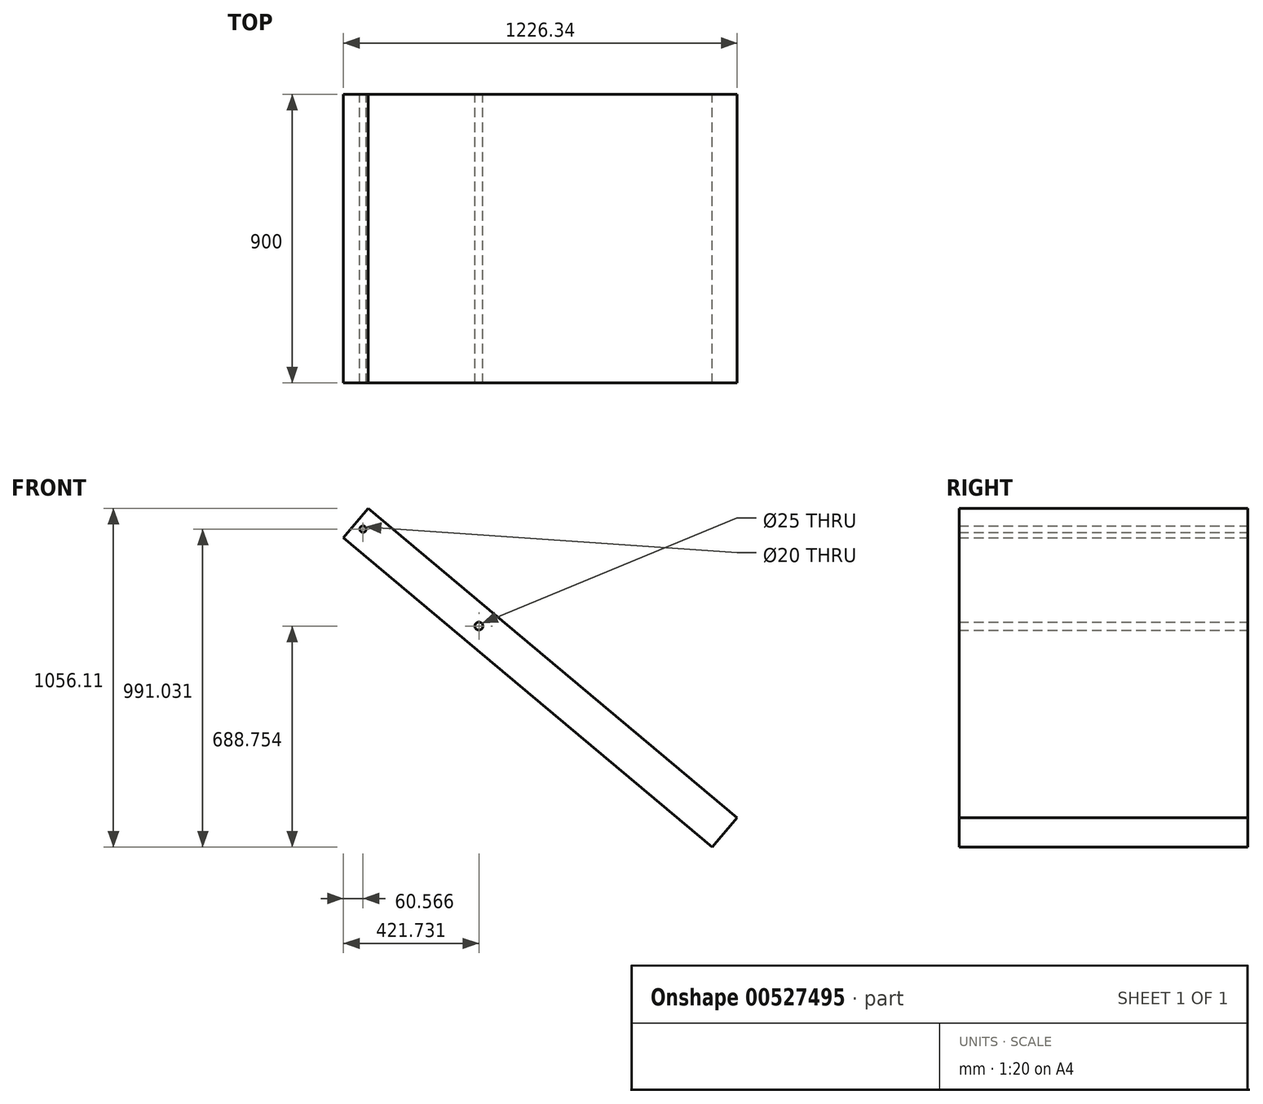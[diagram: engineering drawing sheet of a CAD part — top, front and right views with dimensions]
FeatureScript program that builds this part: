
annotation { "Feature Type Name" : "Feature", "Feature Type Description" : "" }
export const myFeature = defineFeature(function(context is Context, id is Id, definition is map)
    precondition{}
    {
        {
            var Q0;
            Q0=qCreatedBy(makeId("Front.planeOp"),FACE);
            var sketch = newSketch(context, id + "F0", { "sketchPlane" : qUnion([Q0])});
            skLineSegment(sketch, "E0", {"start": v(-23.03, 100) * mm, "end": v(1126.03, -864.18) * mm});
            skLineSegment(sketch, "E1", {"start": v(1126.03, -864.18) * mm, "end": v(1048.9, -956.1) * mm});
            skCircle(sketch, "E2", {"center": v(321.42, -267.36) * mm, "radius": 12.5 * mm});
            skLineSegment(sketch, "E3", {"start": v(-23.03, 100) * mm, "end": v(-100.3, 7.9) * mm});
            skLineSegment(sketch, "E4", {"start": v(-100.3, 7.9) * mm, "end": v(1048.9, -956.1) * mm});
            skCircle(sketch, "E5", {"center": v(-39.74, 34.92) * mm, "radius": 10 * mm});
            skSolve(sketch);
        }
        {
            var Q0;
            Q0=makeQuery(id+"F0.imprint","IMPRINT",FACE,{"disambiguationData":[TD([[makeQuery(id+"F0.imprint","IMPRINT",EDGE,{"derivedFrom":sQuery(id+"F0.wireOp",EDGE,"E0")}),-1.0]])]});
            extrude(context, id + "F1", {"entities" : qUnion([Q0]), "depth" : 900 * mm, "offsetDistance" : 25 * mm});
        }
    });
